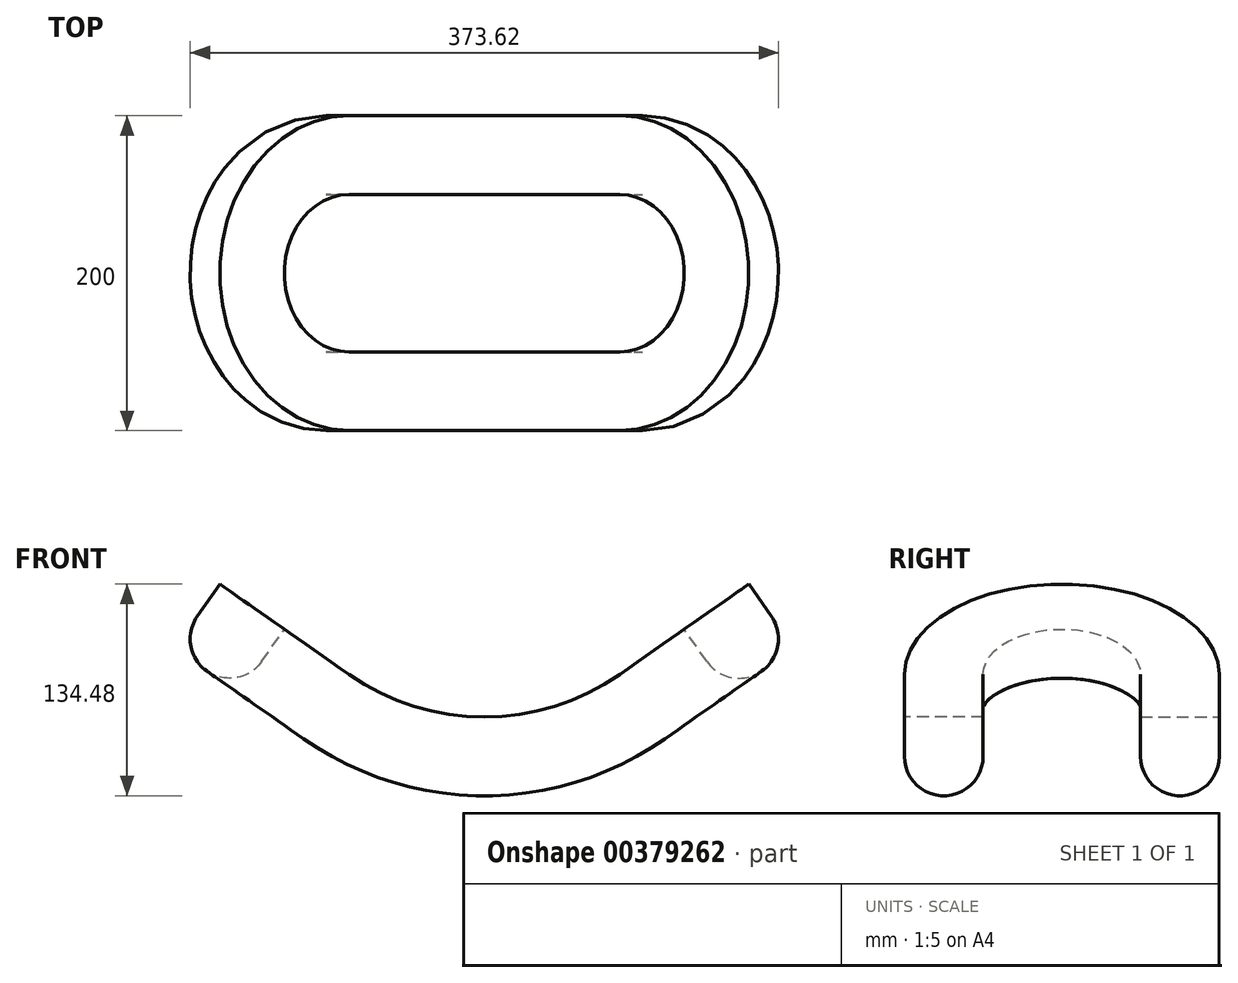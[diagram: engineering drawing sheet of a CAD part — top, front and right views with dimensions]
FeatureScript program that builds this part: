
annotation { "Feature Type Name" : "Feature", "Feature Type Description" : "" }
export const myFeature = defineFeature(function(context is Context, id is Id, definition is map)
    precondition{}
    {
        {
            var Q0;
            Q0=qCreatedBy(makeId("Front.planeOp"),FACE);
            var sketch = newSketch(context, id + "F0", { "sketchPlane" : qUnion([Q0])});
            skArc(sketch, "E0", {"start": v(0, 0) * mm, "mid": v(45.1, 6.94) * mm, "end": v(86.04, 27.13) * mm});
            skLineSegment(sketch, "E1", {"start": v(0, 150) * mm, "end": v(86.04, 27.13) * mm, "construction": true});
            skLineSegment(sketch, "E2", {"start": v(86.04, 27.13) * mm, "end": v(167.95, 84.48) * mm});
            skSolve(sketch);
        }
        {
            var Q0;
            Q0=sQuery(id+"F0.wireOp",EDGE,"E2");
            var Q1;
            Q1=sQuery(id+"F0.wireOp",EDGE,"E0");
            extrude(context, id + "F1", {"bodyType" : ToolBodyType.SURFACE, "surfaceEntities" : qUnion([Q0, Q1]), "depth" : 100 * mm});
        }
        {
            var Q0;
            Q0=makeQuery(id+"F1.opExtrude","SWEPT_FACE",FACE,{"disambiguationData":[OSD([sQuery(id+"F0.wireOp",EDGE,"E2")])]});
            var sketch = newSketch(context, id + "F2", { "sketchPlane" : qUnion([Q0])});
            skArc(sketch, "E3", {"start": v(186.04, 0) * mm, "mid": v(156.75, 70.71) * mm, "end": v(86.04, 100) * mm});
            skSolve(sketch);
        }
        {
            var Q0;
            Q0=qCreatedBy(makeId("Right.planeOp"),FACE);
            var sketch = newSketch(context, id + "F3", { "sketchPlane" : qUnion([Q0])});
            skLineSegment(sketch, "E4.bottom", {"start": v(-50, 0) * mm, "end": v(-100, 0) * mm});
            skLineSegment(sketch, "E4.top", {"start": v(-50, -25) * mm, "end": v(-100, -25) * mm, "construction": true});
            skLineSegment(sketch, "E4.left", {"start": v(-50, 0) * mm, "end": v(-50, -25) * mm});
            skLineSegment(sketch, "E4.right", {"start": v(-100, 0) * mm, "end": v(-100, -25) * mm});
            skArc(sketch, "E5", {"start": v(-100, -25) * mm, "mid": v(-75, -50) * mm, "end": v(-50, -25) * mm});
            skSolve(sketch);
        }
        {
            var Q0;
            Q0=makeQuery(id+"F3.imprint","IMPRINT",FACE,{"disambiguationData":[TD([[makeQuery(id+"F3.imprint","IMPRINT",EDGE,{"derivedFrom":sQuery(id+"F3.wireOp",EDGE,"E4.bottom")}),1.0]])]});
            var Q1;
            Q1=makeQuery(id+"F1.opExtrude","CAP_EDGE",EDGE,{"disambiguationData":[OSD([sQuery(id+"F0.wireOp",EDGE,"E0")])],"isStart":false});
            var Q2;
            Q2=sQuery(id+"F2.wireOp",EDGE,"E3");
            sweep(context, id + "F4", {"profiles" : qUnion([Q0]), "path" : qUnion([Q1, Q2])});
        }
        {
            var Q0;
            Q0=makeQuery(id+"F4.opSweep","SWEPT_BODY",BODY,{"disambiguationData":[OSD([sQuery(id+"F2.wireOp",EDGE,"E3"),sQuery(id+"F3.wireOp",EDGE,"E4.bottom"),sQuery(id+"F3.wireOp",EDGE,"E4.left"),sQuery(id+"F3.wireOp",EDGE,"E4.right"),sQuery(id+"F3.wireOp",EDGE,"E5")])]});
            var Q1;
            Q1=qCreatedBy(makeId("Front.planeOp"),FACE);
            mirror(context, id + "F5", {"operationType" : NewBodyOperationType.ADD, "entities" : qUnion([Q0]), "mirrorPlane" : qUnion([Q1])});
        }
        {
            var Q0;
            Q0=makeQuery(id+"F4.opSweep","SWEPT_BODY",BODY,{"disambiguationData":[OSD([sQuery(id+"F2.wireOp",EDGE,"E3"),sQuery(id+"F3.wireOp",EDGE,"E4.bottom"),sQuery(id+"F3.wireOp",EDGE,"E4.left"),sQuery(id+"F3.wireOp",EDGE,"E4.right"),sQuery(id+"F3.wireOp",EDGE,"E5")])]});
            var Q1;
            Q1=qCreatedBy(makeId("Right.planeOp"),FACE);
            mirror(context, id + "F6", {"operationType" : NewBodyOperationType.ADD, "entities" : qUnion([Q0]), "mirrorPlane" : qUnion([Q1])});
        }
    });
